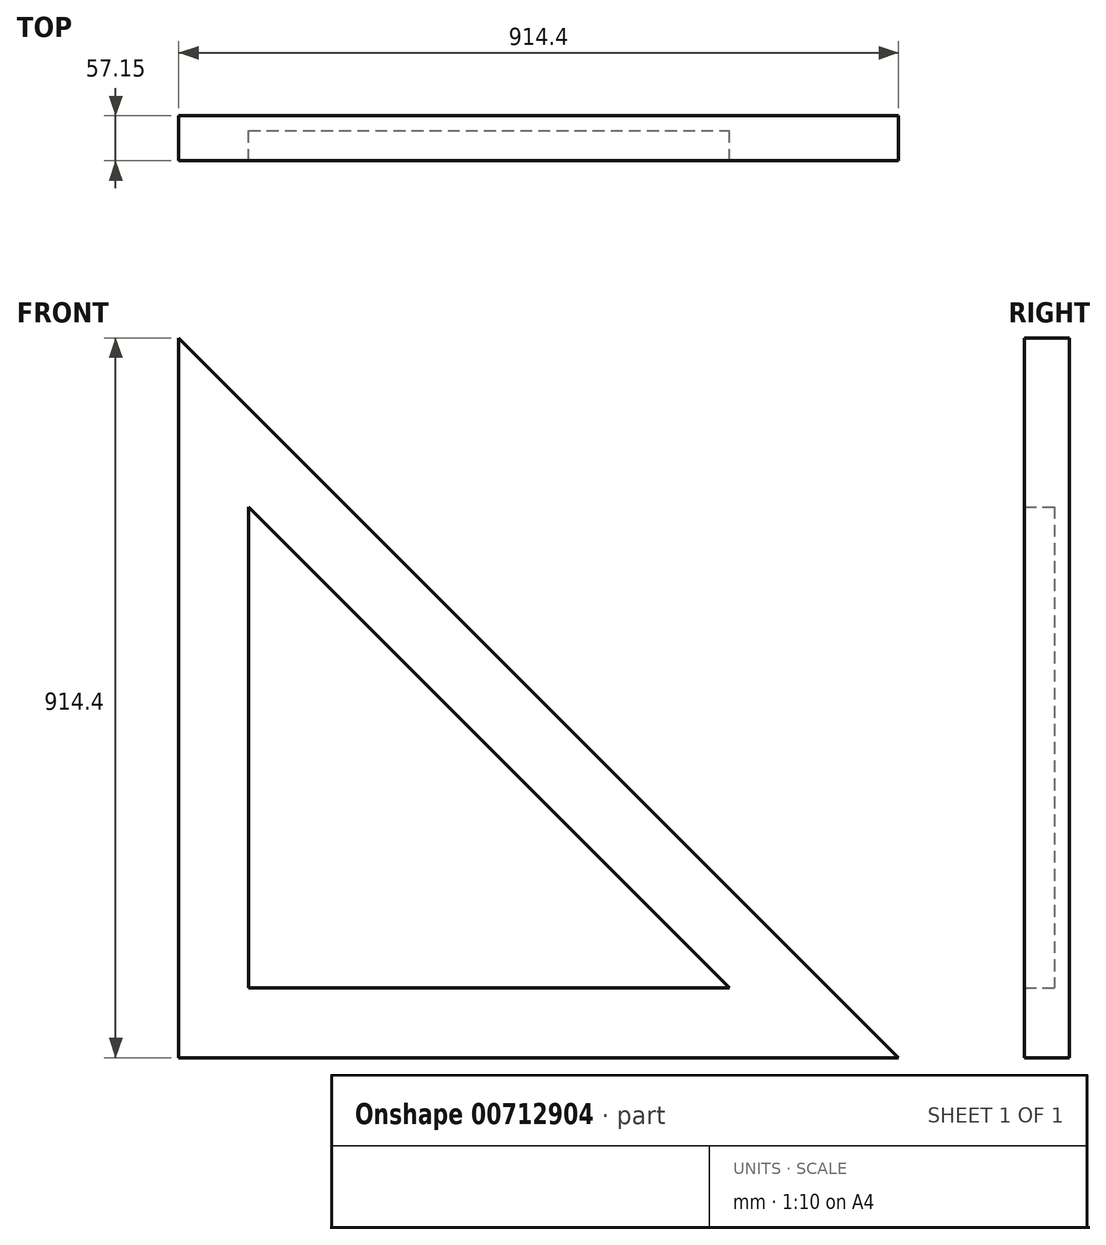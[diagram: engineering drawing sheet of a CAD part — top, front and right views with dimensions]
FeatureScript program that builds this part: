
annotation { "Feature Type Name" : "Feature", "Feature Type Description" : "" }
export const myFeature = defineFeature(function(context is Context, id is Id, definition is map)
    precondition{}
    {
        {
            var Q0;
            Q0=qCreatedBy(makeId("Front.planeOp"),FACE);
            var sketch = newSketch(context, id + "F0", { "sketchPlane" : qUnion([Q0])});
            skLineSegment(sketch, "E0", {"start": v(0, 914.4) * mm, "end": v(914.4, 0) * mm});
            skLineSegment(sketch, "E1", {"start": v(914.4, 0) * mm, "end": v(914.4, 0) * mm});
            skLineSegment(sketch, "E2", {"start": v(0, 0) * mm, "end": v(0, 0) * mm});
            skLineSegment(sketch, "E3", {"start": v(0, 0) * mm, "end": v(914.4, 0) * mm});
            skLineSegment(sketch, "E4", {"start": v(0, 914.4) * mm, "end": v(0, 0) * mm});
            skCircle(sketch, "E5", {"center": v(44.45, 44.45) * mm, "radius": 9.52 * mm});
            skLineSegment(sketch, "E6.0", {"start": v(88.9, 88.9) * mm, "end": v(699.78, 88.9) * mm});
            skLineSegment(sketch, "E6.1", {"start": v(88.9, 699.78) * mm, "end": v(88.9, 88.9) * mm});
            skLineSegment(sketch, "E6.2", {"start": v(88.9, 699.78) * mm, "end": v(699.78, 88.9) * mm});
            skSolve(sketch);
        }
        {
            var Q0;
            Q0=makeQuery(id+"F0.imprint","IMPRINT",FACE,{"disambiguationData":[TD([[makeQuery(id+"F0.imprint","IMPRINT",EDGE,{"derivedFrom":sQuery(id+"F0.wireOp",EDGE,"E0")}),-1.0]])]});
            var Q1;
            Q1=makeQuery(id+"F0.imprint","IMPRINT",FACE,{"disambiguationData":[TD([[makeQuery(id+"F0.imprint","IMPRINT",EDGE,{"derivedFrom":sQuery(id+"F0.wireOp",EDGE,"E5")}),1.0]])]});
            extrude(context, id + "F1", {"entities" : qUnion([Q0, Q1]), "depth" : 38.1 * mm, "offsetDistance" : 25.4 * mm});
        }
        {
            var Q0;
            Q0=makeQuery(id+"F0.imprint","IMPRINT",FACE,{"disambiguationData":[TD([[makeQuery(id+"F0.imprint","IMPRINT",EDGE,{"derivedFrom":sQuery(id+"F0.wireOp",EDGE,"E6.0")}),1.0]])]});
            var Q1;
            Q1=makeQuery(id+"F0.imprint","IMPRINT",FACE,{"disambiguationData":[TD([[makeQuery(id+"F0.imprint","IMPRINT",EDGE,{"derivedFrom":sQuery(id+"F0.wireOp",EDGE,"E0")}),-1.0]])]});
            var Q2;
            Q2=makeQuery(id+"F0.imprint","IMPRINT",FACE,{"disambiguationData":[TD([[makeQuery(id+"F0.imprint","IMPRINT",EDGE,{"derivedFrom":sQuery(id+"F0.wireOp",EDGE,"E5")}),1.0]])]});
            extrude(context, id + "F2", {"entities" : qUnion([Q0, Q1, Q2]), "operationType" : NewBodyOperationType.ADD, "depth" : -19.05 * mm, "offsetDistance" : 25.4 * mm});
        }
    });
